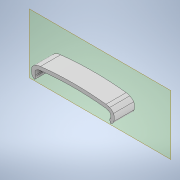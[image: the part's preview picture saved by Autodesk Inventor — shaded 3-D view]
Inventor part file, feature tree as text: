
AUTODESK INVENTOR PART (.ipt)
format: ipt  version: 2021 (Build 250183000, 183)  size: 294,912 bytes
history: native  units: in
note: dims shown in document units (in); Inventor stores cm internally (conversion verified against a paired STEP export)
features: plane x1, extrude x1, sketch x1
ambient origin geometry x8: Origin, YZ Plane, XZ Plane, XY Plane, X Axis, Y Axis, Z Axis, Center Point
bodies: Body1 (feature_tree)
feature tree (3):
  plane  "Work Plane7"
  extrude  "Extrusion3"  Depth=0.7874in
  sketch  "Sketch7"  dims[d20=2.8852in d21=0.1378in d22=2.9463in d23=0.7874in d24=0.0in]
